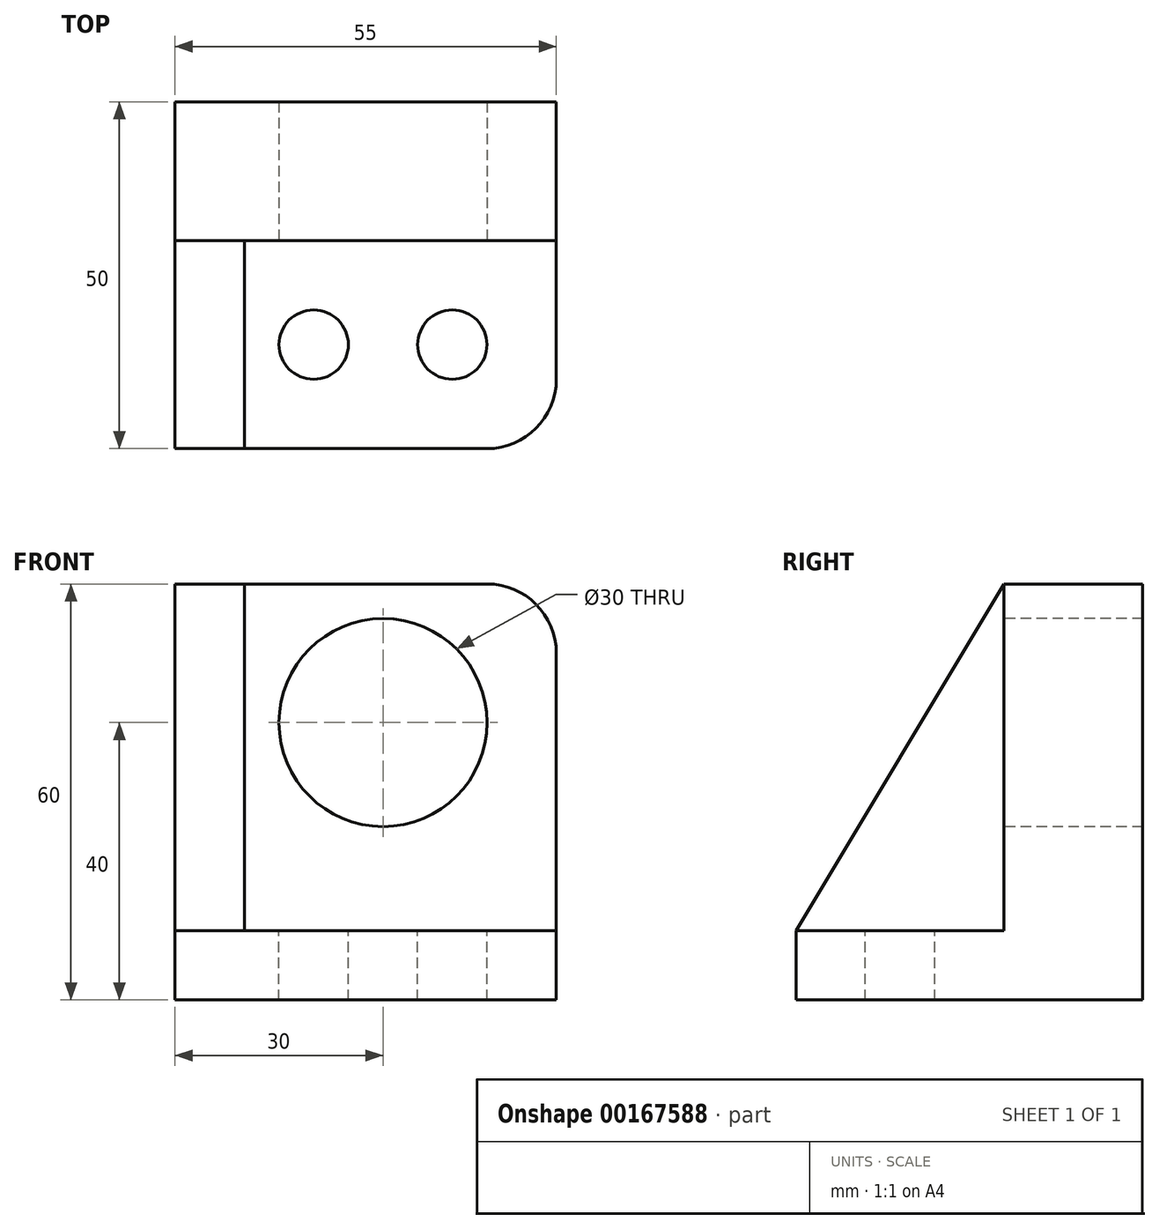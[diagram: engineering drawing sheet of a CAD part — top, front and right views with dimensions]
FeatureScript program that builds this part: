
annotation { "Feature Type Name" : "Feature", "Feature Type Description" : "" }
export const myFeature = defineFeature(function(context is Context, id is Id, definition is map)
    precondition{}
    {
        {
            var Q0;
            Q0=qCreatedBy(makeId("Right.planeOp"),FACE);
            var sketch = newSketch(context, id + "F0", { "sketchPlane" : qUnion([Q0])});
            skLineSegment(sketch, "E0", {"start": v(0, 0) * mm, "end": v(0, 60) * mm});
            skLineSegment(sketch, "E1", {"start": v(0, 60) * mm, "end": v(-20, 60) * mm});
            skLineSegment(sketch, "E2", {"start": v(-20, 60) * mm, "end": v(-20, 10) * mm});
            skLineSegment(sketch, "E3", {"start": v(-20, 10) * mm, "end": v(-50, 10) * mm});
            skLineSegment(sketch, "E4", {"start": v(-50, 10) * mm, "end": v(-50, 0) * mm});
            skLineSegment(sketch, "E5", {"start": v(-50, 0) * mm, "end": v(0, 0) * mm});
            skSolve(sketch);
        }
        {
            var Q0;
            Q0=makeQuery(id+"F0.imprint","IMPRINT",FACE,{"disambiguationData":[TD([[makeQuery(id+"F0.imprint","IMPRINT",EDGE,{"derivedFrom":sQuery(id+"F0.wireOp",EDGE,"E0")}),1.0]])]});
            extrude(context, id + "F1", {"entities" : qUnion([Q0]), "endBound" : BoundingType.SYMMETRIC, "depth" : 55 * mm});
        }
        {
            var Q0;
            Q0=makeQuery(id+"F1.opExtrude","CAP_FACE",FACE,{"disambiguationData":[OSD([sQuery(id+"F0.wireOp",EDGE,"E0"),sQuery(id+"F0.wireOp",EDGE,"E1"),sQuery(id+"F0.wireOp",EDGE,"E2"),sQuery(id+"F0.wireOp",EDGE,"E3"),sQuery(id+"F0.wireOp",EDGE,"E4"),sQuery(id+"F0.wireOp",EDGE,"E5")])],"isStart":true});
            var sketch = newSketch(context, id + "F2", { "sketchPlane" : qUnion([Q0])});
            skLineSegment(sketch, "E6", {"start": v(20, 60) * mm, "end": v(50, 10) * mm});
            skLineSegment(sketch, "E7", {"start": v(50, 10) * mm, "end": v(20, 10) * mm});
            skLineSegment(sketch, "E8", {"start": v(20, 10) * mm, "end": v(20, 60) * mm});
            skSolve(sketch);
        }
        {
            var Q0;
            Q0=makeQuery(id+"F2.imprint","IMPRINT",FACE,{"disambiguationData":[TD([[makeQuery(id+"F2.imprint","IMPRINT",EDGE,{"derivedFrom":sQuery(id+"F2.wireOp",EDGE,"E6")}),-1.0]])]});
            extrude(context, id + "F3", {"entities" : qUnion([Q0]), "operationType" : NewBodyOperationType.ADD, "oppositeDirection" : true, "depth" : 10 * mm});
        }
        {
            var Q0;
            Q0=makeQuery(id+"F1.opExtrude","SWEPT_FACE",FACE,{"disambiguationData":[OSD([sQuery(id+"F0.wireOp",EDGE,"E2")])]});
            var sketch = newSketch(context, id + "F4", { "sketchPlane" : qUnion([Q0])});
            skPoint(sketch, "E9", {"position": v(2.5, 40) * mm});
            skSolve(sketch);
        }
        {
            var Q0;
            Q0=sQuery(id+"F4.wireOp",VERTEX,"E9");
            var Q1;
            Q1=makeQuery(id+"F1.opExtrude","SWEPT_BODY",BODY,{"disambiguationData":[OSD([sQuery(id+"F0.wireOp",EDGE,"E0"),sQuery(id+"F0.wireOp",EDGE,"E1"),sQuery(id+"F0.wireOp",EDGE,"E2"),sQuery(id+"F0.wireOp",EDGE,"E3"),sQuery(id+"F0.wireOp",EDGE,"E4"),sQuery(id+"F0.wireOp",EDGE,"E5")])]});
            hole(context, id + "F5", {"style" : HoleStyle.SIMPLE, "endStyle" : HoleEndStyle.THROUGH, "holeDiameter" : 30 * mm, "locations" : qUnion([Q0]), "scope" : qUnion([Q1]), "isTappedThrough" : true});
        }
        {
            var Q0;
            Q0=makeQuery(id+"F1.opExtrude","SWEPT_FACE",FACE,{"disambiguationData":[OSD([sQuery(id+"F0.wireOp",EDGE,"E3")])]});
            var sketch = newSketch(context, id + "F6", { "sketchPlane" : qUnion([Q0])});
            skPoint(sketch, "E10", {"position": v(12.5, -35) * mm});
            skPoint(sketch, "E11", {"position": v(-7.5, -35) * mm});
            skSolve(sketch);
        }
        {
            var Q0;
            Q0=sQuery(id+"F6.wireOp",VERTEX,"E11");
            var Q1;
            Q1=sQuery(id+"F6.wireOp",VERTEX,"E10");
            var Q2;
            Q2=makeQuery(id+"F1.opExtrude","SWEPT_BODY",BODY,{"disambiguationData":[OSD([sQuery(id+"F0.wireOp",EDGE,"E0"),sQuery(id+"F0.wireOp",EDGE,"E1"),sQuery(id+"F0.wireOp",EDGE,"E2"),sQuery(id+"F0.wireOp",EDGE,"E3"),sQuery(id+"F0.wireOp",EDGE,"E4"),sQuery(id+"F0.wireOp",EDGE,"E5")])]});
            hole(context, id + "F7", {"style" : HoleStyle.SIMPLE, "endStyle" : HoleEndStyle.THROUGH, "holeDiameter" : 10 * mm, "locations" : qUnion([Q0, Q1]), "scope" : qUnion([Q2]), "isTappedThrough" : true});
        }
        {
            var Q0;
            Q0=makeQuery(id+"F1.opExtrude","CAP_EDGE",EDGE,{"disambiguationData":[OSD([sQuery(id+"F0.wireOp",EDGE,"E4")])],"isStart":false});
            fillet(context, id + "F8", {"entities" : qUnion([Q0]), "radius" : 10 * mm, "tangentPropagation" : true, "allowEdgeOverflow" : false});
        }
        {
            var Q0;
            Q0=makeQuery(id+"F1.opExtrude","CAP_EDGE",EDGE,{"disambiguationData":[OSD([sQuery(id+"F0.wireOp",EDGE,"E1")])],"isStart":false});
            fillet(context, id + "F9", {"entities" : qUnion([Q0]), "radius" : 10 * mm, "tangentPropagation" : true, "allowEdgeOverflow" : false});
        }
    });
